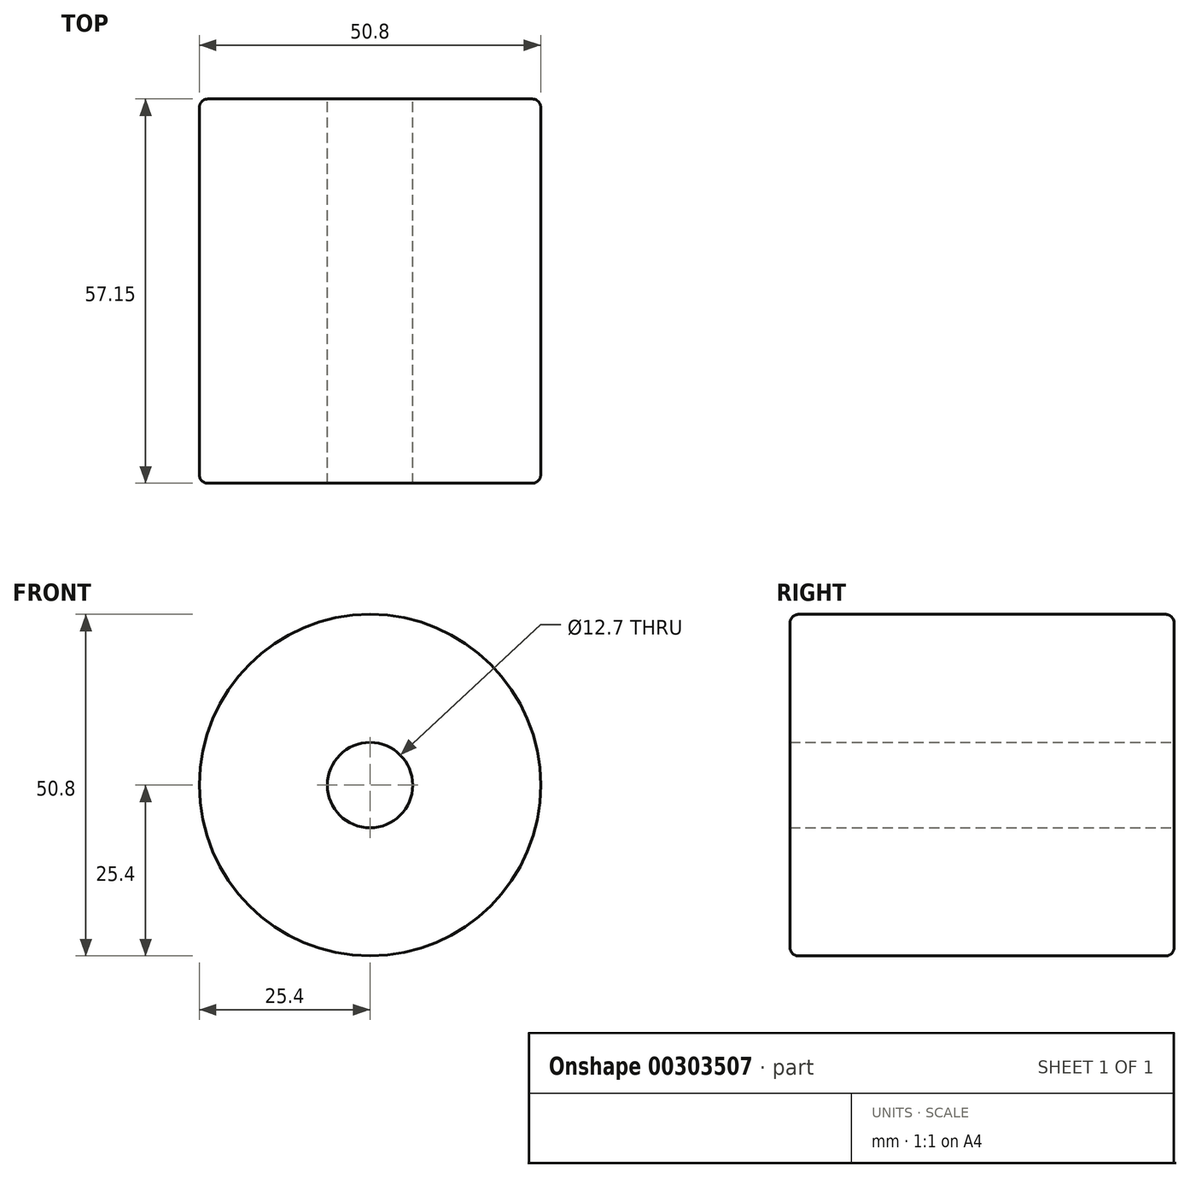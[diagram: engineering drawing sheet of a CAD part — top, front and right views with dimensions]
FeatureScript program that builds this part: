
annotation { "Feature Type Name" : "Feature", "Feature Type Description" : "" }
export const myFeature = defineFeature(function(context is Context, id is Id, definition is map)
    precondition{}
    {
        {
            var Q0;
            Q0=qCreatedBy(makeId("Front.planeOp"),FACE);
            var sketch = newSketch(context, id + "F0", { "sketchPlane" : qUnion([Q0])});
            skCircle(sketch, "E0", {"center": v(0, 0) * mm, "radius": 25.4 * mm});
            skCircle(sketch, "E1", {"center": v(0, 0) * mm, "radius": 6.35 * mm});
            skSolve(sketch);
        }
        {
            var Q0;
            Q0=makeQuery(id+"F0.imprint","IMPRINT",FACE,{"disambiguationData":[TD([[makeQuery(id+"F0.imprint","IMPRINT",EDGE,{"derivedFrom":sQuery(id+"F0.wireOp",EDGE,"E0")}),1.0]])]});
            extrude(context, id + "F1", {"entities" : qUnion([Q0]), "depth" : 57.15 * mm});
        }
        {
            var Q0;
            Q0=makeQuery(id+"F1.opExtrude","CAP_EDGE",EDGE,{"disambiguationData":[OSD([sQuery(id+"F0.wireOp",EDGE,"E0")])],"isStart":true});
            var Q1;
            Q1=makeQuery(id+"F1.opExtrude","CAP_EDGE",EDGE,{"disambiguationData":[OSD([sQuery(id+"F0.wireOp",EDGE,"E0")])],"isStart":false});
            var Q2;
            Q2=makeQuery(id+"F1.opExtrude","SWEPT_FACE",FACE,{"disambiguationData":[OSD([sQuery(id+"F0.wireOp",EDGE,"E0")])]});
            fillet(context, id + "F2", {"entities" : qUnion([Q0, Q1, Q2]), "radius" : 1.27 * mm, "tangentPropagation" : true, "allowEdgeOverflow" : false});
        }
    });
